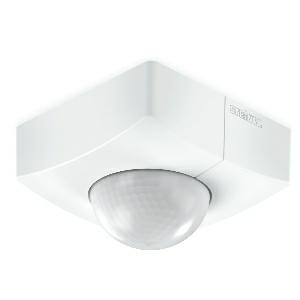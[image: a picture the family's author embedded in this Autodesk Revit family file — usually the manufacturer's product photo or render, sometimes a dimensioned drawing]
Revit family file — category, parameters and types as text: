
# Revit family: is_345_010485
name_source: partatom
category: Elektroinstallationen
revit_build: Autodesk Revit 2016 (Build: 20190508_0715(x64)
units: mm (PartAtom-declared; Revit-internal decimal feet)

## family parameters
Basisbauteil = Fläche
Beim Laden mit Abzugskörper schneiden = Nein
Bemaßung runder Anschluss = Durchmesser verwenden
Beschriftungsausrichtung beibehalten = Nein
Gemeinsam genutzt = Nein
Raumberechnungspunkt = Nein
Teiletyp = Normal

## types (1)
- IS 345
    Apparent Load = 0 VA
    Beschreibung = Type: Motion detectors; Dimensions (L x W x H): 65 x 95 x 95 mm; Mains power supply: 220 – 240 V / 50 – 60 Hz; Sensor Technology: passive infrared; Application, place: Outdoors, Indoors; Application, room: corridor / aisle, multi-storey / underground car park, outdoors, Indoors; Installation site: ceiling; Installation: Surface wiring; Switching zones: 280 switching zones; Electronic scalability: No; Mechanical scalability: No; Mounting height: 2,50 – 5,00 m; Optimum mounting height: 2,8 m; Detection angle: 360 °; Angle of aperture: 45 °; Sneak-by guard: Yes; Capability of masking out individual segments: Yes; Reach, radial: 12 x 6 m (72 m²); Reach, tangential: 23 x 6 m (138 m²); Twilight setting TEACH: Yes; Twilight setting: 2 – 1000 lx; Time setting: 5 sec – 15 min; Switching output 1, resistive: 2000 W; Switching output 1, number of LEDs / fluorescent lamps: 8 pcs.; Constant-lighting control: No; Basic light level function: No; Functions: Normal / test mode, Manual ON / ON-OFF; Settings via: Remote control, Potentiometers, Smart Remote; With remote control: No; Interconnection: Yes; IP-rating: IP54; Material: Plastic; Ambient temperature: -20 – 50 °C; Colour: white; Colour, RAL: 9003; Manufacturer's Warranty: 5 years; Version: COM1 - surface, sq.; PU1, EAN: 4007841010485
    Height = 95 mm
    Hersteller = Steinel
    Length = 65 mm
    Maximum range = 11.589 m
    ModVariant = Nein
    Modell = 010485
    Mounting Place = Ceiling
    Mounting Type = Surface mounted
    Number of Poles = 1
    OnlyDefault = Ja
    Power Factor = 1
    Product Name = IS 345
    Product group = Sensor-switched outdoor light
    ProductGroupID = 3
    Protection Class = Protection class
    Protection Degree = IP 54
    RlxData = <blob elided: 164077 chars, md5=d4b945cc>
    Sensor characteristics = Stretched
    Sensor type = Passive (infrared)
    SensorDataFile = <blob elided: 5885 chars, md5=98bccc25>
    Type of entry = Motion
    Typenbild = produkt1_010485.jpg
    Typenkommentare = Product without accessories
    URL = http://relux.com
    VarID = ---
    Voltage = 0 V
    Vorgabe-Ansicht = 1800 mm
    Weight = 0.00 kg
    Width = 95 mm

## geometry (parser evidence)
native form markers: Blend x4, Sweep x18
no freeform markers — native parametric forms only
